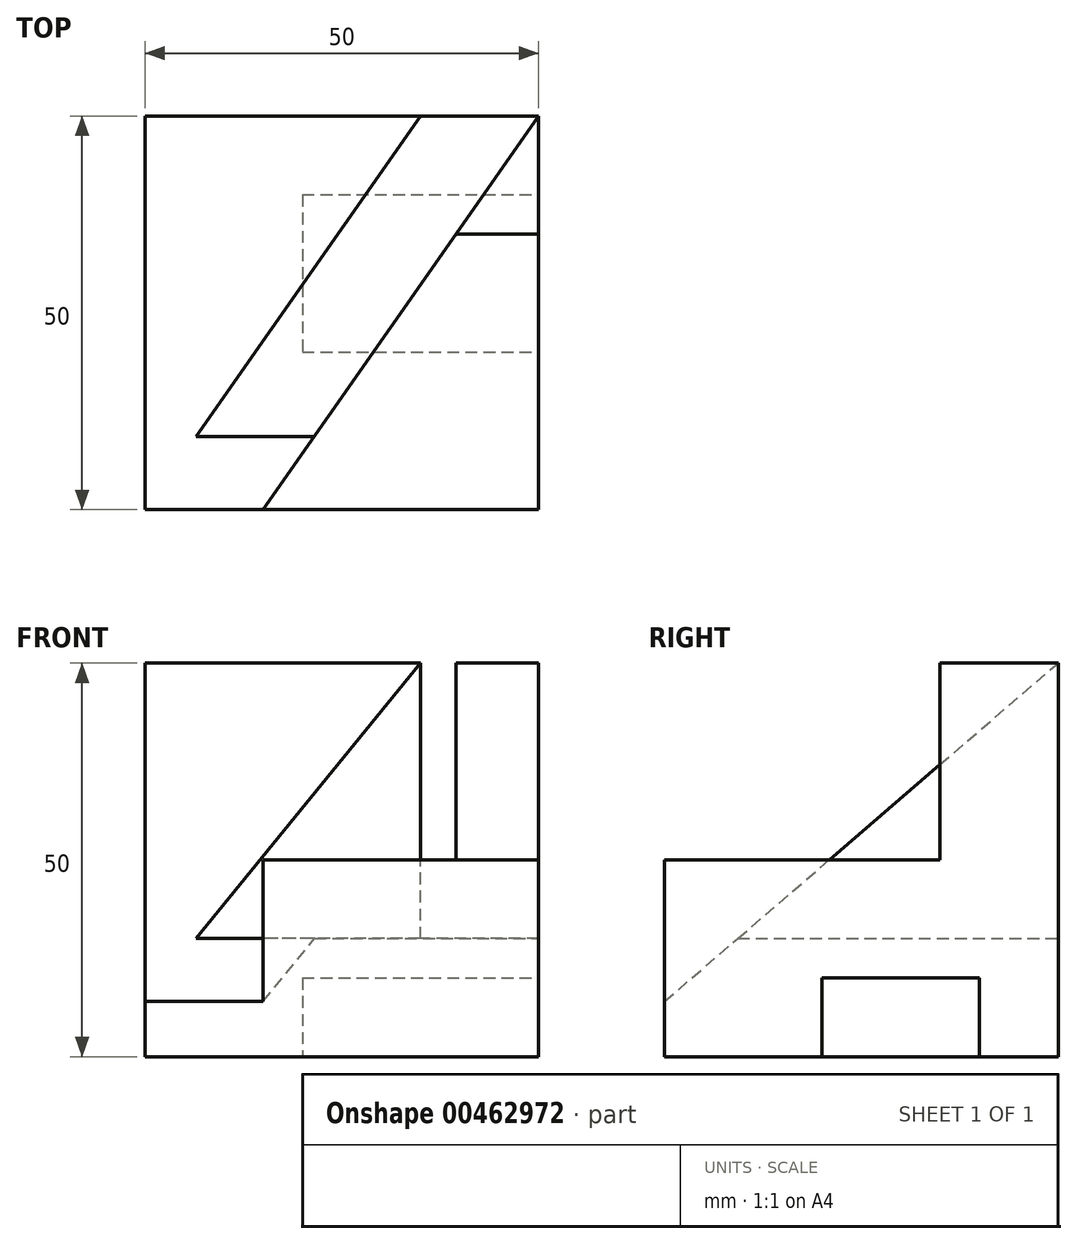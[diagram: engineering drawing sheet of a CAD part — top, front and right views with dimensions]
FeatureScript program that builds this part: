
annotation { "Feature Type Name" : "Feature", "Feature Type Description" : "" }
export const myFeature = defineFeature(function(context is Context, id is Id, definition is map)
    precondition{}
    {
        {
            var Q0;
            Q0=qCreatedBy(makeId("Top.planeOp"),FACE);
            var sketch = newSketch(context, id + "F0", { "sketchPlane" : qUnion([Q0])});
            skLineSegment(sketch, "E0.bottom", {"start": v(-28.9, 34.45) * mm, "end": v(21.1, 34.45) * mm});
            skLineSegment(sketch, "E0.top", {"start": v(-28.9, -15.55) * mm, "end": v(21.1, -15.55) * mm});
            skLineSegment(sketch, "E0.left", {"start": v(-28.9, 34.45) * mm, "end": v(-28.9, -15.55) * mm});
            skLineSegment(sketch, "E0.right", {"start": v(21.1, 34.45) * mm, "end": v(21.1, -15.55) * mm});
            skSolve(sketch);
        }
        {
            var Q0;
            Q0 = qSketchRegion(id + "F0", true);
            extrude(context, id + "F1", {"entities" : qUnion([Q0]), "depth" : 50 * mm});
        }
        {
            var Q0;
            Q0=makeQuery(id+"F1.opExtrude","SWEPT_FACE",FACE,{"disambiguationData":[OSD([sQuery(id+"F0.wireOp",EDGE,"E0.right")])]});
            var sketch = newSketch(context, id + "F2", { "sketchPlane" : qUnion([Q0])});
            skLineSegment(sketch, "E1.bottom", {"start": v(4.45, 10) * mm, "end": v(24.45, 10) * mm});
            skLineSegment(sketch, "E1.top", {"start": v(4.45, 0) * mm, "end": v(24.45, 0) * mm});
            skLineSegment(sketch, "E1.left", {"start": v(4.45, 10) * mm, "end": v(4.45, 0) * mm});
            skLineSegment(sketch, "E1.right", {"start": v(24.45, 10) * mm, "end": v(24.45, 0) * mm});
            skSolve(sketch);
        }
        {
            var Q0;
            Q0=makeQuery(id+"F1.opExtrude","SWEPT_FACE",FACE,{"disambiguationData":[OSD([sQuery(id+"F0.wireOp",EDGE,"E0.left")])]});
            cPlane(context, id + "F3", {"entities" : qUnion([Q0]), "cplaneType" : CPlaneType.OFFSET, "offset" : 20 * mm, "oppositeDirection" : true, "width" : 150 * mm, "height" : 150 * mm});
        }
        {
            var Q0;
            Q0=makeQuery(id+"F2.imprint","IMPRINT",FACE,{"disambiguationData":[TD([[makeQuery(id+"F2.imprint","IMPRINT",EDGE,{"derivedFrom":sQuery(id+"F2.wireOp",EDGE,"E1.bottom")}),-1.0]])]});
            var Q1;
            Q1=qCreatedBy(id+"F3.planeOp",FACE);
            extrude(context, id + "F4", {"entities" : qUnion([Q0]), "operationType" : NewBodyOperationType.REMOVE, "endBound" : BoundingType.UP_TO_SURFACE, "oppositeDirection" : true, "endBoundEntityFace" : qUnion([Q1]), "depth" : 25 * mm});
        }
        {
            var Q0;
            Q0=makeQuery(id+"F1.opExtrude","CAP_FACE",FACE,{"disambiguationData":[OSD([sQuery(id+"F0.wireOp",EDGE,"E0.bottom"),sQuery(id+"F0.wireOp",EDGE,"E0.top"),sQuery(id+"F0.wireOp",EDGE,"E0.left"),sQuery(id+"F0.wireOp",EDGE,"E0.right")])],"isStart":false});
            var sketch = newSketch(context, id + "F5", { "sketchPlane" : qUnion([Q0])});
            skLineSegment(sketch, "E2", {"start": v(21.1, 34.45) * mm, "end": v(-13.9, -15.55) * mm});
            skLineSegment(sketch, "E3", {"start": v(10.6, 19.45) * mm, "end": v(21.1, 19.45) * mm});
            skLineSegment(sketch, "E4", {"start": v(6.1, 34.45) * mm, "end": v(21.1, 34.45) * mm});
            skLineSegment(sketch, "E5", {"start": v(-13.9, -15.55) * mm, "end": v(-28.9, -15.55) * mm});
            skLineSegment(sketch, "E6", {"start": v(-28.9, -15.55) * mm, "end": v(6.1, 34.45) * mm});
            skSolve(sketch);
        }
        {
            var Q0;
            Q0=qCreatedBy(makeId("Top.planeOp"),FACE);
            cPlane(context, id + "F6", {"entities" : qUnion([Q0]), "cplaneType" : CPlaneType.OFFSET, "offset" : 25 * mm, "width" : 150 * mm, "height" : 150 * mm});
        }
        {
            var Q0;
            {var subQ3=sQuery(id+"F5.wireOp",EDGE,"E3");Q0=makeQuery(id+"F5.imprint","IMPRINT",FACE,{"disambiguationData":[TD([[makeQuery(id+"F5.imprint","IMPRINT",EDGE,{"derivedFrom":subQ3}),-1.0]])]});}
            var Q1;
            Q1=qCreatedBy(id+"F6.planeOp",FACE);
            extrude(context, id + "F7", {"entities" : qUnion([Q0]), "operationType" : NewBodyOperationType.REMOVE, "endBound" : BoundingType.UP_TO_SURFACE, "oppositeDirection" : true, "endBoundEntityFace" : qUnion([Q1]), "depth" : 25 * mm});
        }
        {
            var Q0;
            Q0=qCreatedBy(makeId("Top.planeOp"),FACE);
            cPlane(context, id + "F8", {"entities" : qUnion([Q0]), "cplaneType" : CPlaneType.OFFSET, "offset" : 15 * mm, "width" : 150 * mm, "height" : 150 * mm});
        }
        {
            var Q0;
            {var subQ0=sQuery(id+"F5.wireOp",EDGE,"E4");Q0=makeQuery(id+"F5.imprint","IMPRINT",FACE,{"disambiguationData":[TD([[makeQuery(id+"F5.imprint","IMPRINT",EDGE,{"derivedFrom":subQ0}),-1.0]])]});}
            var Q1;
            Q1=qCreatedBy(id+"F8.planeOp",FACE);
            extrude(context, id + "F9", {"entities" : qUnion([Q0]), "operationType" : NewBodyOperationType.REMOVE, "endBound" : BoundingType.UP_TO_SURFACE, "oppositeDirection" : true, "endBoundEntityFace" : qUnion([Q1]), "depth" : 25 * mm});
        }
        {
            var Q0;
            Q0=makeQuery(id+"F1.opExtrude","SWEPT_FACE",FACE,{"disambiguationData":[OSD([sQuery(id+"F0.wireOp",EDGE,"E0.left")])]});
            var sketch = newSketch(context, id + "F10", { "sketchPlane" : qUnion([Q0])});
            skLineSegment(sketch, "E7", {"start": v(15.55, 50) * mm, "end": v(-34.45, 50) * mm});
            skLineSegment(sketch, "E8", {"start": v(-34.45, 50) * mm, "end": v(15.55, 7) * mm});
            skLineSegment(sketch, "E9", {"start": v(15.55, 7) * mm, "end": v(15.55, 50) * mm});
            skSolve(sketch);
        }
        {
            var Q0;
            Q0 = qSketchRegion(id + "F10", true);
            var Q1;
            Q1=makeQuery(id+"F9.boolean.opBoolean","COPY",FACE,{"derivedFrom":makeQuery(id+"F9.opExtrude","SWEPT_FACE",FACE,{"disambiguationData":[OSD([sQuery(id+"F5.wireOp",EDGE,"E2")])]})});
            extrude(context, id + "F11", {"entities" : qUnion([Q0]), "operationType" : NewBodyOperationType.REMOVE, "endBound" : BoundingType.UP_TO_SURFACE, "oppositeDirection" : true, "endBoundEntityFace" : qUnion([Q1]), "depth" : 25 * mm});
        }
    });
